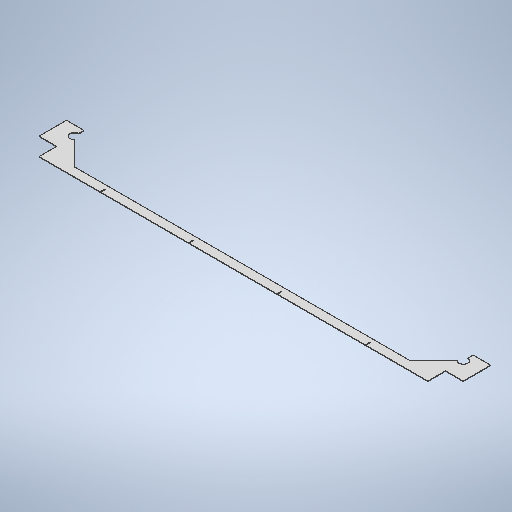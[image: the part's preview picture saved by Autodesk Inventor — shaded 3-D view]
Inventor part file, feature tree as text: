
AUTODESK INVENTOR PART (.ipt)
format: ipt  version: 2025 (Build 290162010, 162A)  size: 333,824 bytes
history: native  units: mm
features: sketch x2, sheet_metal_op x1, extrude x1, mirror x1, pattern_linear x1, other x1
ambient origin geometry x8: Origin, YZ Plane, XZ Plane, XY Plane, X Axis, Y Axis, Z Axis, Center Point
bodies: Solid1 (feature_tree)
feature tree (7):
  sheet_metal_op  "Face1"
  extrude  "Extrusion1"  Depth=3.2mm
  mirror  "Mirror2"
  pattern_linear  "Rectangular Pattern3"  Spacing1=26.0mm  [1 undecoded]
  sketch  "Sketch1"  dims[d2=3.0mm]
  other  "Plate1"
  sketch  "Sketch2"  dims[d3=2400.0mm d4=2900.0mm d5=50.0mm d6=100.0mm d7=50.0mm d8=2644.536997mm d9=135.0deg d10=949.536997mm d11=1149.536997mm d12=23.747141mm d13=50.0mm d14=100.0mm d15=212.786819mm d16=2700.0mm d17=55.0mm d18=200.0mm d19=200.0mm d20=3.2mm d21=26.0mm d22=753.0mm d23=0.0mm d24=0.0mm d31=50.0mm d33=500.0mm]
note: 1 required parameter value undecoded (feature->parameter linkage not recoverable at this tier; creation-order binding heuristic only, values carry confidence <= 0.55)
